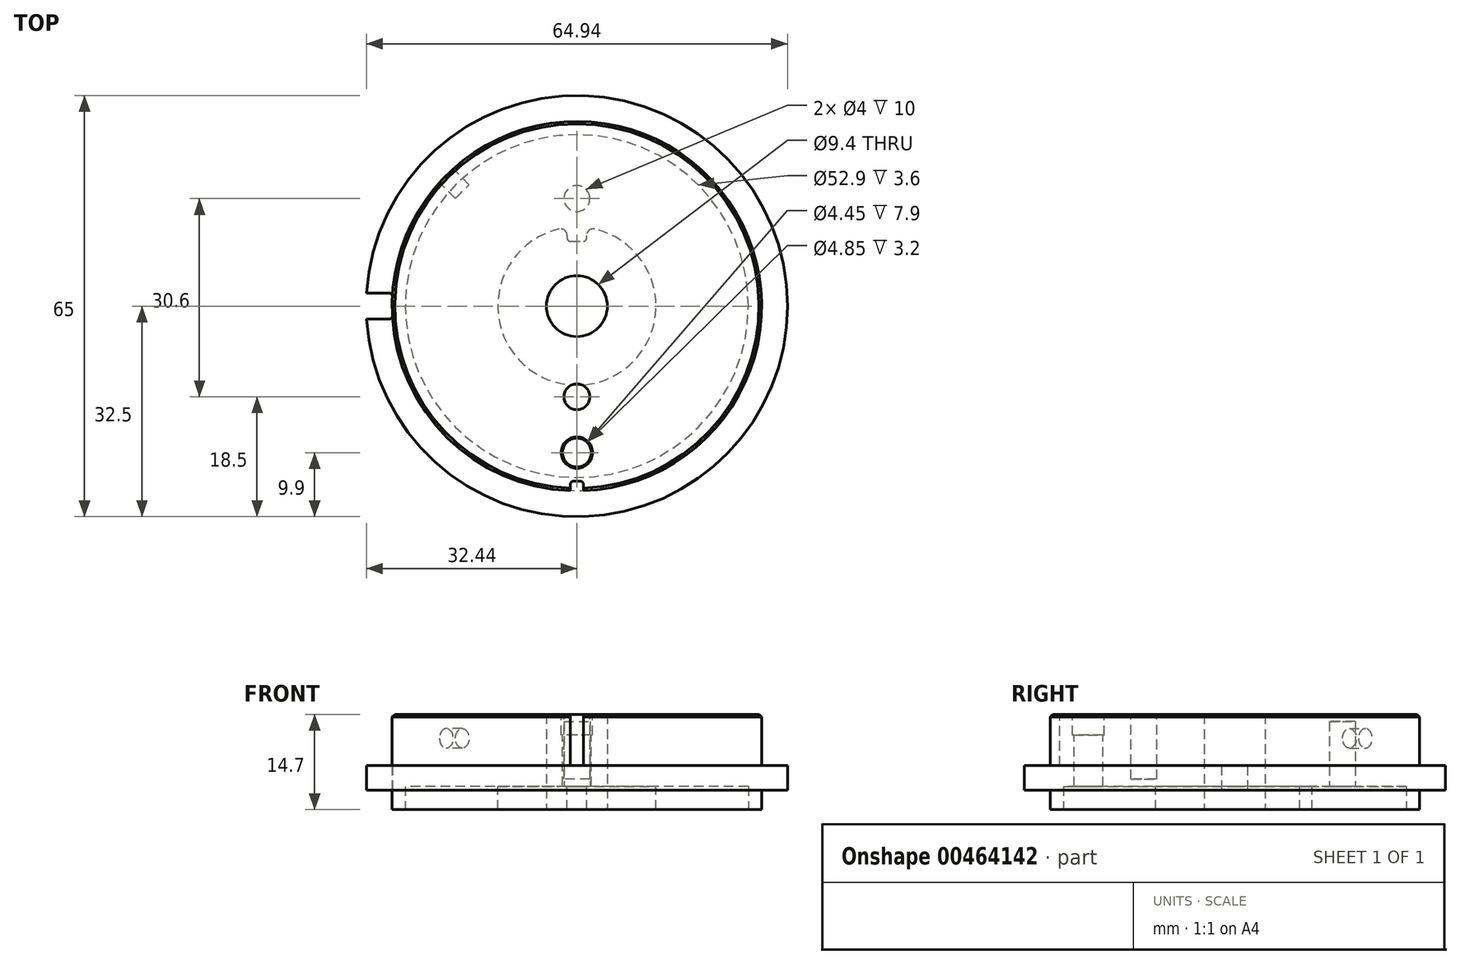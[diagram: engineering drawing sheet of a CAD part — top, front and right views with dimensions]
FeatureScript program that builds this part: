
annotation { "Feature Type Name" : "Feature", "Feature Type Description" : "" }
export const myFeature = defineFeature(function(context is Context, id is Id, definition is map)
    precondition{}
    {
        {
            var Q0;
            Q0=qCreatedBy(makeId("Top.planeOp"),FACE);
            var sketch = newSketch(context, id + "F0", { "sketchPlane" : qUnion([Q0])});
            skCircle(sketch, "E0", {"center": v(0, 0) * mm, "radius": 32.5 * mm});
            skCircle(sketch, "E1", {"center": v(0, 0) * mm, "radius": 28.5 * mm});
            skCircle(sketch, "E2", {"center": v(0, 0) * mm, "radius": 26.45 * mm});
            skCircle(sketch, "E3", {"center": v(0, 0) * mm, "radius": 4.7 * mm});
            skSolve(sketch);
        }
        {
            var Q0;
            Q0=makeQuery(id+"F0.imprint","IMPRINT",FACE,{"disambiguationData":[TD([[makeQuery(id+"F0.imprint","IMPRINT",EDGE,{"derivedFrom":sQuery(id+"F0.wireOp",EDGE,"E1")}),1.0]])]});
            var Q1;
            Q1=makeQuery(id+"F0.imprint","IMPRINT",FACE,{"disambiguationData":[TD([[makeQuery(id+"F0.imprint","IMPRINT",EDGE,{"derivedFrom":sQuery(id+"F0.wireOp",EDGE,"E2")}),1.0]])]});
            extrude(context, id + "F1", {"entities" : qUnion([Q0, Q1]), "depth" : 14.7 * mm, "offsetDistance" : 25 * mm});
        }
        {
            var Q0;
            Q0=makeQuery(id+"F0.imprint","IMPRINT",FACE,{"disambiguationData":[TD([[makeQuery(id+"F0.imprint","IMPRINT",EDGE,{"derivedFrom":sQuery(id+"F0.wireOp",EDGE,"E0")}),1.0]])]});
            extrude(context, id + "F2", {"entities" : qUnion([Q0]), "operationType" : NewBodyOperationType.ADD, "depth" : 6.8 * mm});
        }
        {
            var Q0;
            Q0=makeQuery(id+"F0.imprint","IMPRINT",FACE,{"disambiguationData":[TD([[makeQuery(id+"F0.imprint","IMPRINT",EDGE,{"derivedFrom":sQuery(id+"F0.wireOp",EDGE,"E0")}),1.0]])]});
            extrude(context, id + "F3", {"entities" : qUnion([Q0]), "operationType" : NewBodyOperationType.REMOVE, "depth" : 3 * mm, "offsetDistance" : 25 * mm});
        }
        {
            var Q0;
            Q0=makeQuery(id+"F0.imprint","IMPRINT",FACE,{"disambiguationData":[TD([[makeQuery(id+"F0.imprint","IMPRINT",EDGE,{"derivedFrom":sQuery(id+"F0.wireOp",EDGE,"E2")}),1.0]])]});
            extrude(context, id + "F4", {"entities" : qUnion([Q0]), "operationType" : NewBodyOperationType.REMOVE, "depth" : 3.6 * mm, "offsetDistance" : 25 * mm});
        }
        {
            var Q0;
            Q0=makeQuery(id+"F1.opExtrude","CAP_FACE",FACE,{"disambiguationData":[OSD([sQuery(id+"F0.wireOp",EDGE,"E1"),sQuery(id+"F0.wireOp",EDGE,"E3")])],"isStart":false});
            var sketch = newSketch(context, id + "F5", { "sketchPlane" : qUnion([Q0])});
            skPoint(sketch, "E4", {"position": v(0, -22.6) * mm});
            skSolve(sketch);
        }
        {
            var Q0;
            Q0=sQuery(id+"F5.wireOp",VERTEX,"E4");
            var Q1;
            Q1=makeQuery(id+"F1.opExtrude","SWEPT_BODY",BODY,{"disambiguationData":[OSD([sQuery(id+"F0.wireOp",EDGE,"E1"),sQuery(id+"F0.wireOp",EDGE,"E3")])]});
            hole(context, id + "F6", {"style" : HoleStyle.C_BORE, "endStyle" : HoleEndStyle.THROUGH, "holeDiameter" : 4.45 * mm, "cBoreDiameter" : 4.85 * mm, "cBoreDepth" : 3.2 * mm, "isTappedThrough" : true, "tappedDepth" : 100 * mm, "tapClearance" : 3, "startFromSketch" : true, "locations" : qUnion([Q0]), "scope" : qUnion([Q1]), "majorDiameter" : 5 * mm});
        }
        {
            var Q0;
            Q0=makeQuery(id+"F2.opExtrude","CAP_FACE",FACE,{"disambiguationData":[OSD([sQuery(id+"F0.wireOp",EDGE,"E0"),sQuery(id+"F0.wireOp",EDGE,"E1")])],"isStart":false});
            var sketch = newSketch(context, id + "F7", { "sketchPlane" : qUnion([Q0])});
            skLineSegment(sketch, "E5", {"start": v(-32.44, 2) * mm, "end": v(-28.43, 2) * mm});
            skLineSegment(sketch, "E6", {"start": v(-32.44, -2) * mm, "end": v(-28.43, -2) * mm});
            skCircle(sketch, "E7.0", {"center": v(0, 0) * mm, "radius": 28.5 * mm});
            skCircle(sketch, "E8.0", {"center": v(0, 0) * mm, "radius": 32.5 * mm});
            skSolve(sketch);
        }
        {
            var Q0;
            {var subQ0=sQuery(id+"F7.wireOp",EDGE,"E5");Q0=makeQuery(id+"F7.imprint","IMPRINT",FACE,{"disambiguationData":[TD([[makeQuery(id+"F7.imprint","IMPRINT",EDGE,{"derivedFrom":subQ0}),-1.0]])]});}
            extrude(context, id + "F8", {"entities" : qUnion([Q0]), "operationType" : NewBodyOperationType.REMOVE, "endBound" : BoundingType.THROUGH_ALL, "oppositeDirection" : true, "depth" : 25 * mm, "offsetDistance" : 25 * mm});
        }
        {
            var Q0;
            Q0=makeQuery(id+"F1.opExtrude","CAP_FACE",FACE,{"disambiguationData":[OSD([sQuery(id+"F0.wireOp",EDGE,"E1"),sQuery(id+"F0.wireOp",EDGE,"E3")])],"isStart":false});
            var sketch = newSketch(context, id + "F9", { "sketchPlane" : qUnion([Q0])});
            skLineSegment(sketch, "E9", {"start": v(-1, -27) * mm, "end": v(1, -27) * mm});
            skLineSegment(sketch, "E10", {"start": v(1, -27) * mm, "end": v(1, -28.48) * mm});
            skLineSegment(sketch, "E11", {"start": v(-1, -27) * mm, "end": v(-1, -28.48) * mm});
            skCircle(sketch, "E12.0", {"center": v(0, 0) * mm, "radius": 28.5 * mm});
            skSolve(sketch);
        }
        {
            var Q0;
            Q0=makeQuery(id+"F9.imprint","IMPRINT",FACE,{"disambiguationData":[TD([[makeQuery(id+"F9.imprint","IMPRINT",EDGE,{"derivedFrom":sQuery(id+"F9.wireOp",EDGE,"E9")}),-1.0]])]});
            var Q1;
            Q1=makeQuery(id+"F2.opExtrude","CAP_FACE",FACE,{"disambiguationData":[OSD([sQuery(id+"F0.wireOp",EDGE,"E0"),sQuery(id+"F0.wireOp",EDGE,"E1")])],"isStart":false});
            extrude(context, id + "F10", {"entities" : qUnion([Q0]), "operationType" : NewBodyOperationType.REMOVE, "endBound" : BoundingType.UP_TO_SURFACE, "oppositeDirection" : true, "endBoundEntityFace" : qUnion([Q1]), "depth" : 25 * mm, "offsetDistance" : 25 * mm});
        }
        {
            var Q0;
            Q0=makeQuery(id+"F1.opExtrude","CAP_FACE",FACE,{"disambiguationData":[OSD([sQuery(id+"F0.wireOp",EDGE,"E1"),sQuery(id+"F0.wireOp",EDGE,"E3")])],"isStart":false});
            var sketch = newSketch(context, id + "F11", { "sketchPlane" : qUnion([Q0])});
            skPoint(sketch, "E13.0", {"position": v(0, 0) * mm});
            skArc(sketch, "E14.0", {"start": v(1, -28.48) * mm, "mid": v(0, 28.5) * mm, "end": v(-1, -28.48) * mm});
            skLineSegment(sketch, "E15", {"start": v(0, 0) * mm, "end": v(-20.15, 20.15) * mm, "construction": true});
            skSolve(sketch);
        }
        {
            var Q0;
            Q0=sQuery(id+"F11.wireOp",EDGE,"E15");
            var Q1;
            Q1=sQuery(id+"F11.wireOp",VERTEX,"E15.end");
            cPlane(context, id + "F12", {"entities" : qUnion([Q0, Q1]), "cplaneType" : CPlaneType.LINE_POINT, "offset" : 25 * mm, "width" : 150 * mm, "height" : 150 * mm});
        }
        {
            var Q0;
            Q0=qCreatedBy(id+"F12.planeOp",FACE);
            var sketch = newSketch(context, id + "F13", { "sketchPlane" : qUnion([Q0])});
            skPoint(sketch, "E16.0", {"position": v(0, 14.7) * mm});
            skPoint(sketch, "E17", {"position": v(0, 11) * mm});
            skCircle(sketch, "E18", {"center": v(0, 11) * mm, "radius": 1.5 * mm});
            skSolve(sketch);
        }
        {
            var Q0;
            Q0=makeQuery(id+"F13.imprint","IMPRINT",FACE,{"disambiguationData":[TD([[makeQuery(id+"F13.imprint","IMPRINT",EDGE,{"derivedFrom":sQuery(id+"F13.wireOp",EDGE,"E18")}),1.0]])]});
            var Q1;
            Q1=sQuery(id+"F13.wireOp",EDGE,"E18");
            extrude(context, id + "F14", {"entities" : qUnion([Q0]), "operationType" : NewBodyOperationType.REMOVE, "surfaceEntities" : qUnion([Q1]), "oppositeDirection" : true, "depth" : 3.5 * mm, "offsetDistance" : 25 * mm});
        }
        {
            var Q0;
            Q0=makeQuery(id+"F4.boolean.opBoolean","COPY",FACE,{"derivedFrom":makeQuery(id+"F4.opExtrude","CAP_FACE",FACE,{"disambiguationData":[OSD([sQuery(id+"F0.wireOp",EDGE,"E2"),sQuery(id+"F0.wireOp",EDGE,"E3")])],"isStart":false})});
            var sketch = newSketch(context, id + "F15", { "sketchPlane" : qUnion([Q0])});
            skPoint(sketch, "E19", {"position": v(0, -16.6) * mm});
            skCircle(sketch, "E20", {"center": v(0, -16.6) * mm, "radius": 2 * mm});
            skSolve(sketch);
        }
        {
            var Q0;
            Q0=makeQuery(id+"F15.imprint","IMPRINT",FACE,{"disambiguationData":[TD([[makeQuery(id+"F15.imprint","IMPRINT",EDGE,{"derivedFrom":sQuery(id+"F15.wireOp",EDGE,"E20")}),1.0]])]});
            extrude(context, id + "F16", {"entities" : qUnion([Q0]), "operationType" : NewBodyOperationType.REMOVE, "oppositeDirection" : true, "depth" : 10 * mm, "offsetDistance" : 25 * mm});
        }
        {
            var Q0;
            Q0=makeQuery(id+"F11.imprint","IMPRINT",FACE,{"disambiguationData":[TD([[makeQuery(id+"F11.imprint","IMPRINT",EDGE,{"derivedFrom":sQuery(id+"F11.wireOp",EDGE,"E14.0")}),1.0]])]});
            var sketch = newSketch(context, id + "F17", { "sketchPlane" : qUnion([Q0])});
            skPoint(sketch, "E21", {"position": v(0, -14) * mm});
            skCircle(sketch, "E22", {"center": v(0, -14) * mm, "radius": 2 * mm});
            skSolve(sketch);
        }
        {
            var Q0;
            Q0=makeQuery(id+"F4.boolean.opBoolean","COPY",FACE,{"derivedFrom":makeQuery(id+"F4.opExtrude","CAP_FACE",FACE,{"disambiguationData":[OSD([sQuery(id+"F0.wireOp",EDGE,"E2"),sQuery(id+"F0.wireOp",EDGE,"E3")])],"isStart":false})});
            var sketch = newSketch(context, id + "F18", { "sketchPlane" : qUnion([Q0])});
            skCircle(sketch, "E23", {"center": v(0, 0) * mm, "radius": 12.2 * mm});
            skCircle(sketch, "E24.0", {"center": v(0, 0) * mm, "radius": 4.7 * mm});
            skLineSegment(sketch, "E25", {"start": v(-1.5, -12.1) * mm, "end": v(-1.5, -10) * mm});
            skLineSegment(sketch, "E26", {"start": v(-1.5, -10) * mm, "end": v(1.5, -10) * mm});
            skLineSegment(sketch, "E27", {"start": v(1.5, -10) * mm, "end": v(1.5, -12.1) * mm});
            skSolve(sketch);
        }
        {
            var Q0;
            Q0=makeQuery(id+"F18.imprint","IMPRINT",FACE,{"disambiguationData":[TD([[makeQuery(id+"F18.imprint","IMPRINT",EDGE,{"derivedFrom":sQuery(id+"F18.wireOp",EDGE,"E24.0")}),1.0]])]});
            var Q1;
            {var subQ5=makeQuery(id+"FBLP35QzhvjIRWv_1.boolean.opBoolean","COPY",EDGE,{"derivedFrom":makeQuery(id+"FBLP35QzhvjIRWv_1.opExtrude","CAP_EDGE",EDGE,{"disambiguationData":[OSD([sQuery(id+"F17.wireOp",EDGE,"7d91854b-4f5c-40d7-a3fa-28e83b9ded65.3")])],"isStart":true})});Q1=makeQuery(id+"F18.imprint","IMPRINT",FACE,{"disambiguationData":[TD([[makeQuery(id+"F18.imprint","IMPRINT",EDGE,{"derivedFrom":subQ5}),-1.0]])]});}
            var Q2;
            {var subQ5=makeQuery(id+"F2WvY61BHToyDlE_1.1.FBLP35QzhvjIRWv_1.boolean.opBoolean","COPY",EDGE,{"derivedFrom":makeQuery(id+"F2WvY61BHToyDlE_1.1.FBLP35QzhvjIRWv_1.opExtrude","CAP_EDGE",EDGE,{"disambiguationData":[OSD([sQuery(id+"F17.wireOp",EDGE,"7d91854b-4f5c-40d7-a3fa-28e83b9ded65.3")])],"isStart":true})});Q2=makeQuery(id+"F18.imprint","IMPRINT",FACE,{"disambiguationData":[TD([[makeQuery(id+"F18.imprint","IMPRINT",EDGE,{"derivedFrom":subQ5}),-1.0]])]});}
            var Q3;
            {var subQ5=makeQuery(id+"F2WvY61BHToyDlE_1.2.FBLP35QzhvjIRWv_1.boolean.opBoolean","COPY",EDGE,{"derivedFrom":makeQuery(id+"F2WvY61BHToyDlE_1.2.FBLP35QzhvjIRWv_1.opExtrude","CAP_EDGE",EDGE,{"disambiguationData":[OSD([sQuery(id+"F17.wireOp",EDGE,"7d91854b-4f5c-40d7-a3fa-28e83b9ded65.3")])],"isStart":true})});Q3=makeQuery(id+"F18.imprint","IMPRINT",FACE,{"disambiguationData":[TD([[makeQuery(id+"F18.imprint","IMPRINT",EDGE,{"derivedFrom":subQ5}),-1.0]])]});}
            var Q4;
            {var subQ0=sQuery(id+"F0.wireOp",EDGE,"E1");Q4=makeQuery(id+"F2.boolean.opBoolean","MERGE",FACE,{"derivedFrom":[makeQuery(id+"F1.opExtrude","CAP_FACE",FACE,{"disambiguationData":[OSD([subQ0,sQuery(id+"F0.wireOp",EDGE,"E3")])],"isStart":true}),makeQuery(id+"F2.opExtrude","CAP_FACE",FACE,{"disambiguationData":[OSD([sQuery(id+"F0.wireOp",EDGE,"E0"),subQ0])],"isStart":true})]});}
            extrude(context, id + "F19", {"entities" : qUnion([Q0, Q1, Q2, Q3]), "operationType" : NewBodyOperationType.ADD, "endBound" : BoundingType.UP_TO_SURFACE, "endBoundEntityFace" : qUnion([Q4]), "depth" : 25 * mm, "offsetDistance" : 25 * mm});
        }
        {
            var Q0;
            Q0=makeQuery(id+"F17.imprint","IMPRINT",FACE,{"disambiguationData":[TD([[makeQuery(id+"F17.imprint","IMPRINT",EDGE,{"derivedFrom":sQuery(id+"F17.wireOp",EDGE,"E22")}),1.0]])]});
            extrude(context, id + "F20", {"entities" : qUnion([Q0]), "operationType" : NewBodyOperationType.REMOVE, "oppositeDirection" : true, "depth" : 10 * mm, "offsetDistance" : 25 * mm});
        }
        {
            var Q0;
            Q0=makeQuery(id+"F1.opExtrude","CAP_EDGE",EDGE,{"disambiguationData":[OSD([sQuery(id+"F0.wireOp",EDGE,"E1")])],"isStart":false});
            var Q1;
            Q1=makeQuery(id+"F3.boolean.opBoolean","COPY",EDGE,{"derivedFrom":makeQuery(id+"F3.opExtrude","CAP_EDGE",EDGE,{"disambiguationData":[OSD([sQuery(id+"F0.wireOp",EDGE,"E0")])],"isStart":false})});
            chamfer(context, id + "F21", {"entities" : qUnion([Q0, Q1]), "width" : .4 * mm, "tangentPropagation" : true});
        }
        {
            var Q0;
            Q0=makeQuery(id+"F8.boolean.opBoolean","COPY",EDGE,{"derivedFrom":makeQuery(id+"F8.opExtrude","SWEPT_EDGE",EDGE,{"disambiguationData":[OSD([sQuery(id+"F7.wireOp",EDGE,"E5"),sQuery(id+"F7.wireOp",EDGE,"E8.0")])]})});
            var Q1;
            Q1=makeQuery(id+"F8.boolean.opBoolean","COPY",EDGE,{"derivedFrom":makeQuery(id+"F8.opExtrude","SWEPT_EDGE",EDGE,{"disambiguationData":[OSD([sQuery(id+"F7.wireOp",EDGE,"E6"),sQuery(id+"F7.wireOp",EDGE,"E8.0")])]})});
            var Q2;
            Q2=makeQuery(id+"F19.opExtrude","SWEPT_EDGE",EDGE,{"disambiguationData":[OSD([sQuery(id+"F18.wireOp",EDGE,"E23"),sQuery(id+"F18.wireOp",EDGE,"E25")])]});
            var Q3;
            Q3=makeQuery(id+"F19.opExtrude","SWEPT_EDGE",EDGE,{"disambiguationData":[OSD([sQuery(id+"F18.wireOp",EDGE,"E23"),sQuery(id+"F18.wireOp",EDGE,"E27")])]});
            fillet(context, id + "F22", {"entities" : qUnion([Q0, Q1, Q2, Q3]), "radius" : 1 * mm, "tangentPropagation" : true, "allowEdgeOverflow" : false});
        }
        {
            var Q0;
            Q0=makeQuery(id+"F10.boolean.opBoolean","COPY",EDGE,{"derivedFrom":makeQuery(id+"F10.opExtrude","SWEPT_EDGE",EDGE,{"disambiguationData":[OSD([sQuery(id+"F9.wireOp",EDGE,"E9"),sQuery(id+"F9.wireOp",EDGE,"E10")])]})});
            var Q1;
            Q1=makeQuery(id+"F10.boolean.opBoolean","COPY",EDGE,{"derivedFrom":makeQuery(id+"F10.opExtrude","SWEPT_EDGE",EDGE,{"disambiguationData":[OSD([sQuery(id+"F9.wireOp",EDGE,"E9"),sQuery(id+"F9.wireOp",EDGE,"E11")])]})});
            fillet(context, id + "F23", {"entities" : qUnion([Q0, Q1]), "radius" : .5 * mm, "tangentPropagation" : true, "allowEdgeOverflow" : false});
        }
        {
            var Q0;
            Q0=makeQuery(id+"F19.opExtrude","SWEPT_EDGE",EDGE,{"disambiguationData":[OSD([sQuery(id+"F18.wireOp",EDGE,"E25"),sQuery(id+"F18.wireOp",EDGE,"E26")])]});
            var Q1;
            Q1=makeQuery(id+"F19.opExtrude","SWEPT_EDGE",EDGE,{"disambiguationData":[OSD([sQuery(id+"F18.wireOp",EDGE,"E26"),sQuery(id+"F18.wireOp",EDGE,"E27")])]});
            fillet(context, id + "F24", {"entities" : qUnion([Q0, Q1]), "radius" : .5 * mm, "tangentPropagation" : true, "allowEdgeOverflow" : false});
        }
        {
            var Q0;
            Q0=makeQuery(id+"F8.boolean.opBoolean","COPY",EDGE,{"derivedFrom":makeQuery(id+"F8.opExtrude","SWEPT_EDGE",EDGE,{"disambiguationData":[OSD([sQuery(id+"F7.wireOp",EDGE,"E5"),sQuery(id+"F7.wireOp",EDGE,"E7.0")])]})});
            var Q1;
            Q1=makeQuery(id+"F8.boolean.opBoolean","COPY",EDGE,{"derivedFrom":makeQuery(id+"F8.opExtrude","SWEPT_EDGE",EDGE,{"disambiguationData":[OSD([sQuery(id+"F7.wireOp",EDGE,"E6"),sQuery(id+"F7.wireOp",EDGE,"E7.0")])]})});
            var Q2;
            Q2=makeQuery(id+"F19.opExtrude","SWEPT_EDGE",EDGE,{"disambiguationData":[OSD([sQuery(id+"F18.wireOp",EDGE,"E25"),sQuery(id+"F18.wireOp",EDGE,"E26")])]});
            var Q3;
            Q3=makeQuery(id+"F19.opExtrude","SWEPT_EDGE",EDGE,{"disambiguationData":[OSD([sQuery(id+"F18.wireOp",EDGE,"E26"),sQuery(id+"F18.wireOp",EDGE,"E27")])]});
            fillet(context, id + "F25", {"entities" : qUnion([Q0, Q1, Q2, Q3]), "radius" : .5 * mm, "tangentPropagation" : true, "allowEdgeOverflow" : false});
        }
    });
